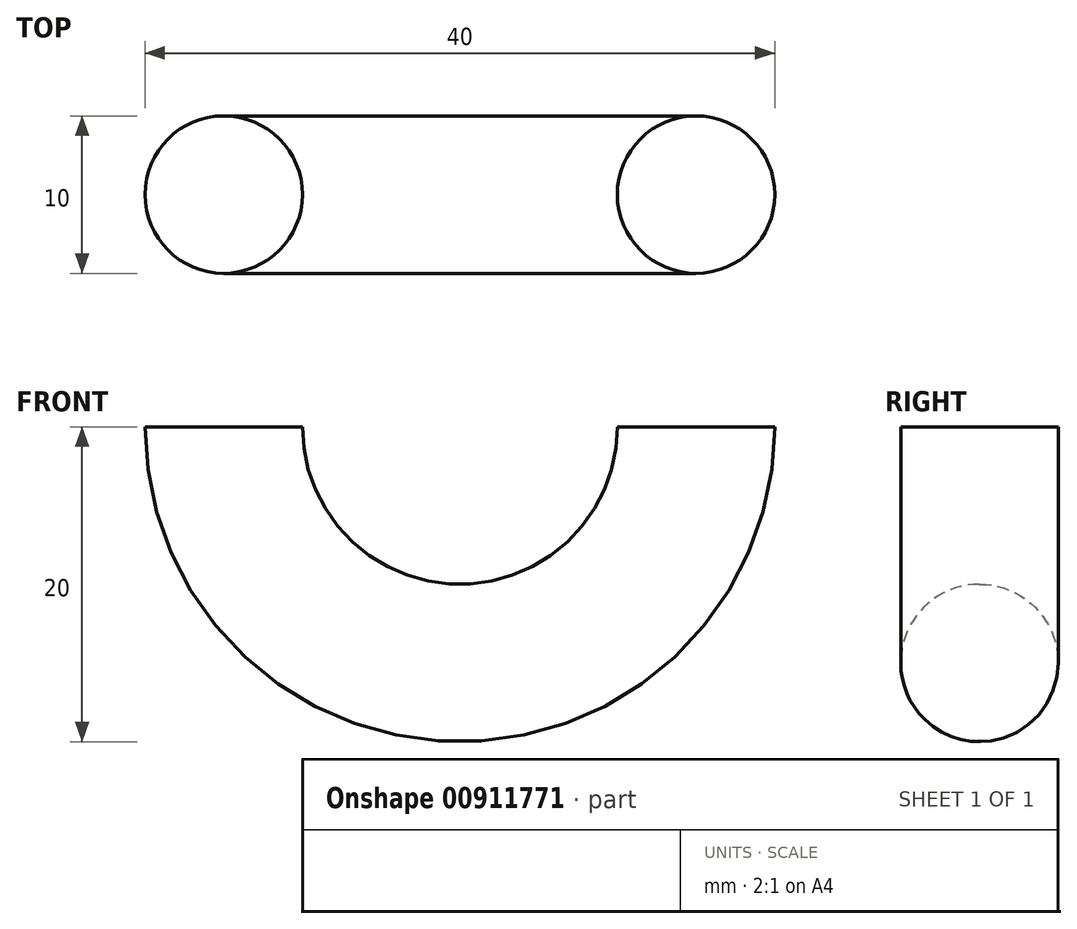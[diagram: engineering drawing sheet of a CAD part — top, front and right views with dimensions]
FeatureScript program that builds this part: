
annotation { "Feature Type Name" : "Feature", "Feature Type Description" : "" }
export const myFeature = defineFeature(function(context is Context, id is Id, definition is map)
    precondition{}
    {
        {
            var Q0;
            Q0=qCreatedBy(makeId("Top.planeOp"),FACE);
            var sketch = newSketch(context, id + "F0", { "sketchPlane" : qUnion([Q0])});
            skPoint(sketch, "E0", {"position": v(-15, 0) * mm});
            skCircle(sketch, "E1", {"center": v(-15, 0) * mm, "radius": 5 * mm});
            skPoint(sketch, "E2", {"position": v(15, 0) * mm});
            skCircle(sketch, "E3", {"center": v(15, 0) * mm, "radius": 5 * mm});
            skLineSegment(sketch, "E4", {"start": v(0, 27.1) * mm, "end": v(0, -38.1) * mm});
            skSolve(sketch);
        }
        {
            var Q0;
            Q0=makeQuery(id+"F0.imprint","IMPRINT",FACE,{"disambiguationData":[TD([[makeQuery(id+"F0.imprint","IMPRINT",EDGE,{"derivedFrom":sQuery(id+"F0.wireOp",EDGE,"E1")}),1.0]])]});
            var Q1;
            Q1=sQuery(id+"F0.wireOp",EDGE,"E4");
            revolve(context, id + "F1", {"surfaceOperationType" : NewSurfaceOperationType.NEW, "entities" : qUnion([Q0]), "axis" : qUnion([Q1]), "revolveType" : RevolveType.ONE_DIRECTION, "angle" : 180 * degree});
        }
    });
